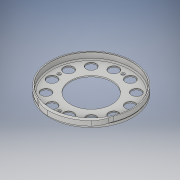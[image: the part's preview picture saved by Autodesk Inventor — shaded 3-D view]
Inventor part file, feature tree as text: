
AUTODESK INVENTOR PART (.ipt)
format: ipt  version: 2018 (Build 220112000, 112)  size: 273,920 bytes
history: native  units: mm
features: sketch x3, extrude x3, hole x2, chamfer x2, pattern_circular x2, fillet x2, revolve x1, other x1, projected_geometry x1
ambient origin geometry x8: Origin, YZ Plane, XZ Plane, XY Plane, X Axis, Y Axis, Z Axis, Center Point
bodies: Solid1 (feature_tree)
feature tree (17):
  sketch  "Sketch1"  dims[d0=35.0mm d1=68.0mm]
  extrude  "Extrusion1"  Depth=35.0mm
  extrude  "Extrusion2"  Depth=72.0mm
  extrude  "Extrusion3"  Depth=0.2mm
  revolve  "Revolution1"  [1 undecoded]
  sketch  "Sketch3"  dims[d4=32.36mm d5=1.06mm d6=5.14mm d7=26.16mm d8=10.3mm d9=1.54mm d10=16.74mm d11=26.16mm d12=37.0mm d13=33.97mm d14=33.07mm d15=13.335mm d16=20.0mm d17=19.0mm d18=37.0mm d19=19.0mm d20=20.0mm d21=20.0mm d22=6.5mm d23=0.0mm d24=5.5mm d25=0.0mm d26=2.5mm d27=0.0mm d28=0.5mm d29=2.0mm d30=0.25mm d31=90.0deg d32=54.0mm d33=27.0mm d35=6.99mm d36=8.0mm d37=6.0mm d38=4.0mm d39=2.0mm d40=90.0deg d41=27.0mm d42=0.0mm d43=2.0mm d44=6.0mm d45=4.0mm d46=2.0mm d47=90.0deg d48=27.0mm d49=0.0mm d50=0.5mm d51=2.0mm d52=45.0deg d53=0.2mm d54=2.0mm d55=45.0deg d56=120.0mm d57=360.0deg d59=30.0mm d60=180.0deg d62=1.0mm d63=0.2mm]
  hole  "Hole1"  [1 undecoded]
  hole  "Hole2"  [1 undecoded]
  chamfer  "Chamfer1"  Distance=1.54mm
  chamfer  "Chamfer2"  Distance=16.74mm
  other  "Work Axis1"
  pattern_circular  "Circular Pattern1"  [2 undecoded]
  pattern_circular  "Circular Pattern2"  [2 undecoded]
  fillet  "Fillet1"  Radius=33.97mm
  fillet  "Fillet2"  Radius=33.07mm
  sketch  "Sketch2"  dims[d2=70.0mm d3=72.0mm]
  projected_geometry  "Project Cut Edges1"
note: 7 required parameter values undecoded (feature->parameter linkage not recoverable at this tier; creation-order binding heuristic only, values carry confidence <= 0.55)